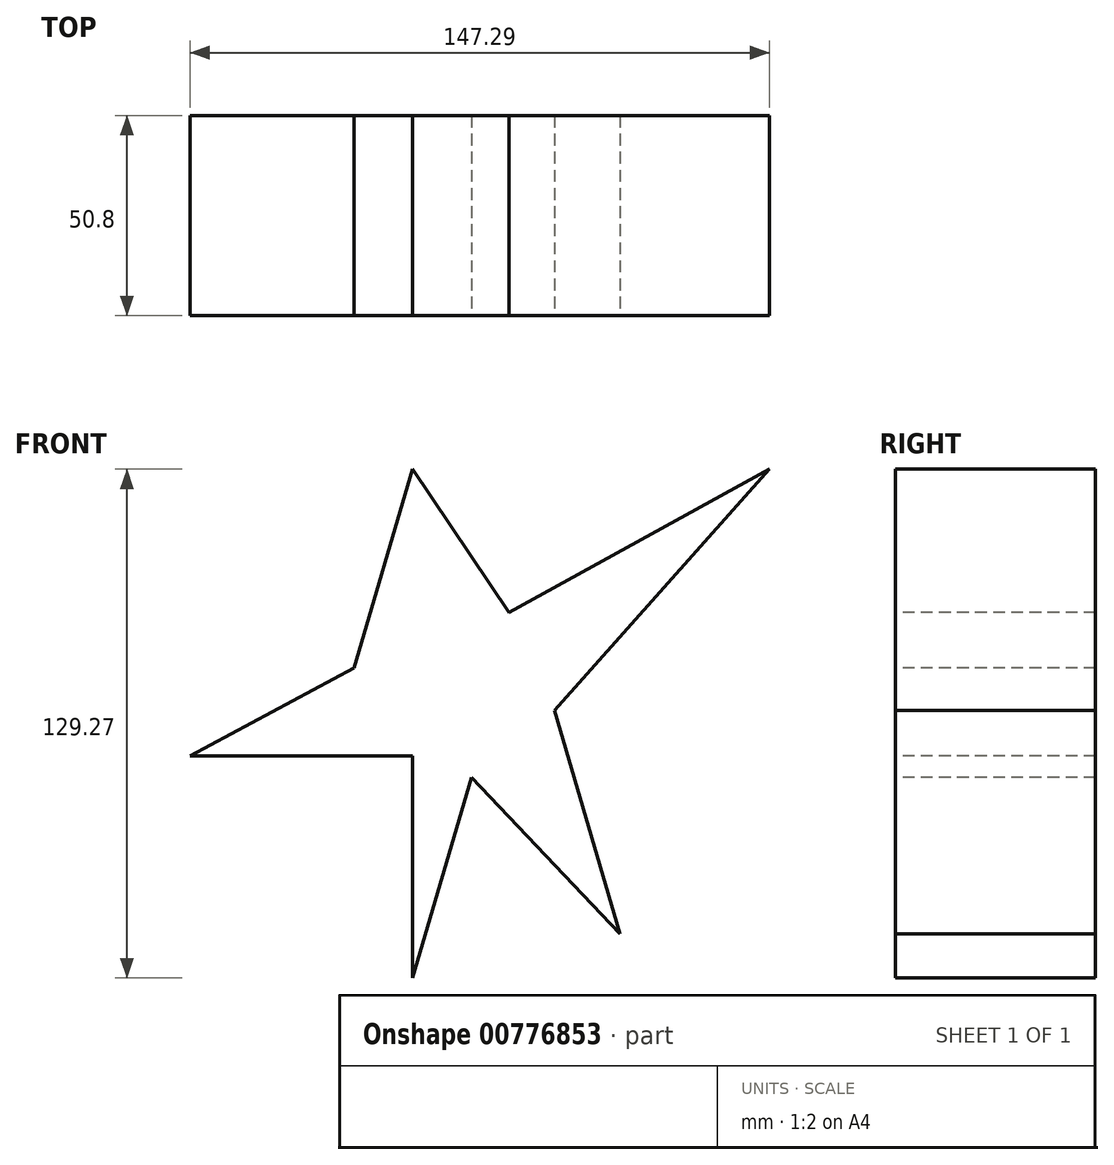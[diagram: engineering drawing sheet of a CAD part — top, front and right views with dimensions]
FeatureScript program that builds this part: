
annotation { "Feature Type Name" : "Feature", "Feature Type Description" : "" }
export const myFeature = defineFeature(function(context is Context, id is Id, definition is map)
    precondition{}
    {
        {
            var Q0;
            Q0=qCreatedBy(makeId("Front.planeOp"),FACE);
            var sketch = newSketch(context, id + "F0", { "sketchPlane" : qUnion([Q0])});
            skLineSegment(sketch, "E0", {"start": v(0, 0) * mm, "end": v(15, 50.91) * mm});
            skLineSegment(sketch, "E1", {"start": v(15, 50.91) * mm, "end": v(52.7, 11.18) * mm});
            skLineSegment(sketch, "E2", {"start": v(52.7, 11.18) * mm, "end": v(36, 67.98) * mm});
            skLineSegment(sketch, "E3", {"start": v(36, 67.98) * mm, "end": v(90.7, 129.27) * mm});
            skLineSegment(sketch, "E4", {"start": v(90.7, 129.27) * mm, "end": v(24.48, 92.88) * mm});
            skLineSegment(sketch, "E5", {"start": v(24.48, 92.88) * mm, "end": v(0, 129.27) * mm});
            skLineSegment(sketch, "E6", {"start": v(0, 129.27) * mm, "end": v(-14.9, 78.69) * mm});
            skLineSegment(sketch, "E7", {"start": v(-14.9, 78.69) * mm, "end": v(-56.6, 56.38) * mm});
            skLineSegment(sketch, "E8", {"start": v(-56.6, 56.38) * mm, "end": v(0, 56.38) * mm});
            skLineSegment(sketch, "E9", {"start": v(0, 56.38) * mm, "end": v(0, 0) * mm});
            skSolve(sketch);
        }
        {
            var Q0;
            Q0=makeQuery(id+"F0.imprint","IMPRINT",FACE,{"disambiguationData":[TD([[makeQuery(id+"F0.imprint","IMPRINT",EDGE,{"derivedFrom":sQuery(id+"F0.wireOp",EDGE,"E0")}),1.0]])]});
            extrude(context, id + "F1", {"entities" : qUnion([Q0]), "oppositeDirection" : true, "depth" : 50.8 * mm, "offsetDistance" : 25.4 * mm});
        }
    });
